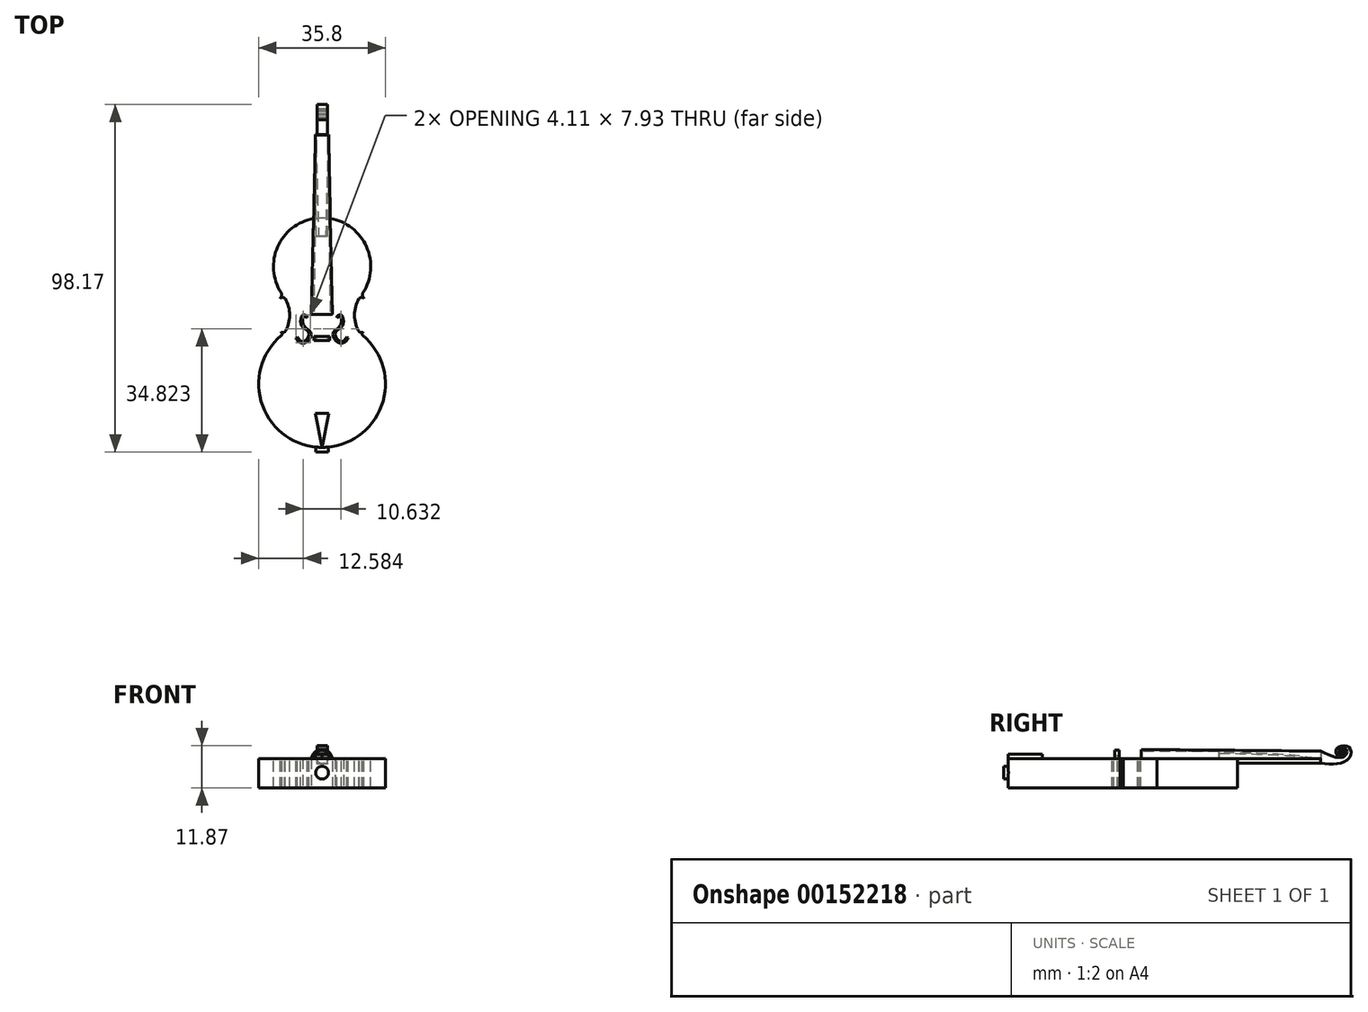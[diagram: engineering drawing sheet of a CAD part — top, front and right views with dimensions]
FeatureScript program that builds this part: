
annotation { "Feature Type Name" : "Feature", "Feature Type Description" : "" }
export const myFeature = defineFeature(function(context is Context, id is Id, definition is map)
    precondition{}
    {
        {
            var Q0;
            Q0=qCreatedBy(makeId("Top.planeOp"),FACE);
            var sketch = newSketch(context, id + "F0", { "sketchPlane" : qUnion([Q0])});
            skArc(sketch, "E0", {"start": v(11.58, 16.32) * mm, "mid": v(0, 37.44) * mm, "end": v(-11.58, 16.32) * mm});
            skArc(sketch, "E1", {"start": v(10.46, 14.69) * mm, "mid": v(9.16, 9.93) * mm, "end": v(10.53, 5.2) * mm});
            skArc(sketch, "E2", {"start": v(-10.53, 5.2) * mm, "mid": v(-9.16, 9.93) * mm, "end": v(-10.46, 14.69) * mm});
            skArc(sketch, "E3", {"start": v(-11.48, 4.23) * mm, "mid": v(0, -27.4) * mm, "end": v(11.48, 4.23) * mm});
            skLineSegment(sketch, "E4", {"start": v(0, -27.4) * mm, "end": v(0, -9.5) * mm, "construction": true});
            skPoint(sketch, "E4.startSnap0", {"position": v(0, -27.4) * mm});
            skLineSegment(sketch, "E5", {"start": v(-3.69, 4.75) * mm, "end": v(-3.08, 4.75) * mm, "construction": true});
            skFitSpline(sketch, "E6", {"points": [v(-4.15, 9.6) * mm, v(-5.44, 10.01) * mm, v(-5.83, 7.1) * mm, v(-3.69, 4.75) * mm, v(-5.3, 2.5) * mm, v(-6.98, 3.84) * mm], "startDerivative": vector(-11.64, 6.4) * mm, "endDerivative": vector(-7.15, 13.02) * mm});
            skFitSpline(sketch, "E7.MirrorCS", {"points": [v(4.15, 9.6) * mm, v(5.44, 10.01) * mm, v(5.83, 7.1) * mm, v(3.69, 4.75) * mm, v(5.3, 2.5) * mm, v(6.98, 3.84) * mm], "startDerivative": vector(11.64, 6.4) * mm, "endDerivative": vector(7.15, 13.02) * mm});
            skLineSegment(sketch, "E8", {"start": v(-4.15, 9.6) * mm, "end": v(-4.15, 9.2) * mm});
            skFitSpline(sketch, "E9", {"points": [v(-4.15, 9.2) * mm, v(-5.28, 9.33) * mm, v(-5.11, 6.98) * mm, v(-3.08, 4.75) * mm, v(-5.3, 1.97) * mm, v(-7.37, 3.53) * mm], "startDerivative": vector(-11.64, 6.4) * mm, "endDerivative": vector(-1.06, 6.87) * mm});
            skLineSegment(sketch, "E10", {"start": v(-7.37, 3.53) * mm, "end": v(-6.98, 3.84) * mm});
            skFitSpline(sketch, "E11.MirrorCS", {"points": [v(4.15, 9.2) * mm, v(5.28, 9.33) * mm, v(5.11, 6.98) * mm, v(3.08, 4.75) * mm, v(5.3, 1.97) * mm, v(7.37, 3.53) * mm], "startDerivative": vector(11.64, 6.4) * mm, "endDerivative": vector(1.06, 6.87) * mm});
            skLineSegment(sketch, "E12.MirrorCS", {"start": v(7.37, 3.53) * mm, "end": v(6.98, 3.84) * mm});
            skLineSegment(sketch, "E13.MirrorCS", {"start": v(4.15, 9.6) * mm, "end": v(4.15, 9.2) * mm});
            skArc(sketch, "E14", {"start": v(-11.9, 14.69) * mm, "mid": v(-11.41, 15.44) * mm, "end": v(-11.58, 16.32) * mm});
            skArc(sketch, "E15", {"start": v(-10.46, 14.69) * mm, "mid": v(-11.18, 14.93) * mm, "end": v(-11.9, 14.69) * mm});
            skArc(sketch, "E16.MirrorCS", {"start": v(11.9, 14.69) * mm, "mid": v(11.41, 15.44) * mm, "end": v(11.58, 16.32) * mm});
            skArc(sketch, "E17.MirrorCS", {"start": v(10.46, 14.69) * mm, "mid": v(11.18, 14.93) * mm, "end": v(11.9, 14.69) * mm});
            skArc(sketch, "E18", {"start": v(-11.53, 4.18) * mm, "mid": v(-11.31, 4.76) * mm, "end": v(-11.76, 5.2) * mm});
            skArc(sketch, "E19", {"start": v(-11.76, 5.2) * mm, "mid": v(-11.14, 5.08) * mm, "end": v(-10.53, 5.2) * mm});
            skArc(sketch, "E20.MirrorCS", {"start": v(11.76, 5.2) * mm, "mid": v(11.14, 5.08) * mm, "end": v(10.53, 5.2) * mm});
            skArc(sketch, "E21.MirrorCS", {"start": v(11.53, 4.18) * mm, "mid": v(11.31, 4.76) * mm, "end": v(11.76, 5.2) * mm});
            skPoint(sketch, "E22.start.orphan", {"position": v(-10.83, 15.26) * mm});
            skLineSegment(sketch, "E23.trimOffspring", {"start": v(3.08, 4.75) * mm, "end": v(3.69, 4.75) * mm, "construction": true});
            skPoint(sketch, "E24.orphan", {"position": v(-10.83, 4.75) * mm});
            skSolve(sketch);
        }
        {
            var Q0;
            Q0=makeQuery(id+"F0.imprint","IMPRINT",FACE,{"disambiguationData":[TD([[makeQuery(id+"F0.imprint","IMPRINT",EDGE,{"derivedFrom":sQuery(id+"F0.wireOp",EDGE,"E0")}),1.0]])]});
            extrude(context, id + "F1", {"entities" : qUnion([Q0]), "oppositeDirection" : true, "depth" : 8.25 * mm});
        }
        {
            var Q0;
            Q0=makeQuery(id+"F0.imprint","IMPRINT",FACE,{"disambiguationData":[TD([[makeQuery(id+"F0.imprint","IMPRINT",EDGE,{"derivedFrom":sQuery(id+"F0.wireOp",EDGE,"E6")}),1.0]])]});
            extrude(context, id + "F2", {"entities" : qUnion([Q0]), "operationType" : NewBodyOperationType.REMOVE, "oppositeDirection" : true, "depth" : 25.4 * mm});
        }
        {
            var Q0;
            Q0=makeQuery(id+"F1.opExtrude","CAP_FACE",FACE,{"disambiguationData":[OSD([sQuery(id+"F0.wireOp",EDGE,"E0"),sQuery(id+"F0.wireOp",EDGE,"E1"),sQuery(id+"F0.wireOp",EDGE,"E2"),sQuery(id+"F0.wireOp",EDGE,"E3"),sQuery(id+"F0.wireOp",EDGE,"E6"),sQuery(id+"F0.wireOp",EDGE,"E7.MirrorCS"),sQuery(id+"F0.wireOp",EDGE,"E8"),sQuery(id+"F0.wireOp",EDGE,"E9"),sQuery(id+"F0.wireOp",EDGE,"E10"),sQuery(id+"F0.wireOp",EDGE,"E11.MirrorCS"),sQuery(id+"F0.wireOp",EDGE,"E12.MirrorCS"),sQuery(id+"F0.wireOp",EDGE,"E13.MirrorCS")])],"isStart":true});
            var sketch = newSketch(context, id + "F3", { "sketchPlane" : qUnion([Q0])});
            skLineSegment(sketch, "E25.bottom", {"start": v(-2.8, 3.95) * mm, "end": v(2.8, 3.95) * mm});
            skLineSegment(sketch, "E25.top", {"start": v(-2.8, 3.43) * mm, "end": v(2.8, 3.43) * mm});
            skLineSegment(sketch, "E25.left", {"start": v(-2.8, 3.95) * mm, "end": v(-2.8, 3.43) * mm});
            skLineSegment(sketch, "E25.right", {"start": v(2.8, 3.95) * mm, "end": v(2.8, 3.43) * mm});
            skLineSegment(sketch, "E26", {"start": v(0, 0) * mm, "end": v(0, 3.95) * mm, "construction": true});
            skSolve(sketch);
        }
        {
            var Q0;
            Q0=makeQuery(id+"F3.imprint","IMPRINT",FACE,{"disambiguationData":[TD([[makeQuery(id+"F3.imprint","IMPRINT",EDGE,{"derivedFrom":sQuery(id+"F3.wireOp",EDGE,"E25.bottom")}),-1.0]])]});
            extrude(context, id + "F4", {"entities" : qUnion([Q0]), "operationType" : NewBodyOperationType.ADD, "depth" : 2.73 * mm});
        }
        {
            var Q0;
            Q0=makeQuery(id+"F4.opExtrude","SWEPT_FACE",FACE,{"disambiguationData":[OSD([sQuery(id+"F3.wireOp",EDGE,"E25.top")])]});
            var sketch = newSketch(context, id + "F5", { "sketchPlane" : qUnion([Q0])});
            skArc(sketch, "E27", {"start": v(1.52, 0) * mm, "mid": v(-0.1, 0.76) * mm, "end": v(-1.7, 0) * mm});
            skSolve(sketch);
        }
        {
            var Q0;
            {var subQ0=sQuery(id+"F5.wireOp",EDGE,"E27");Q0=makeQuery(id+"F5.imprint","IMPRINT",FACE,{"disambiguationData":[TD([[makeQuery(id+"F5.imprint","IMPRINT",EDGE,{"derivedFrom":subQ0}),1.0]])]});}
            extrude(context, id + "F6", {"entities" : qUnion([Q0]), "operationType" : NewBodyOperationType.REMOVE, "oppositeDirection" : true, "depth" : 25.4 * mm});
        }
        {
            var Q0;
            Q0=makeQuery(id+"F4.opExtrude","SWEPT_FACE",FACE,{"disambiguationData":[OSD([sQuery(id+"F3.wireOp",EDGE,"E25.top")])]});
            var sketch = newSketch(context, id + "F7", { "sketchPlane" : qUnion([Q0])});
            skArc(sketch, "E28", {"start": v(2.15, 0) * mm, "mid": v(-0.05, 2.36) * mm, "end": v(-2.25, 0) * mm});
            skSolve(sketch);
        }
        {
            var Q0;
            {var subQ0=sQuery(id+"F7.wireOp",EDGE,"E28");Q0=makeQuery(id+"F7.imprint","IMPRINT",FACE,{"disambiguationData":[TD([[makeQuery(id+"F7.imprint","IMPRINT",EDGE,{"derivedFrom":subQ0}),1.0]])]});}
            extrude(context, id + "F8", {"entities" : qUnion([Q0]), "operationType" : NewBodyOperationType.ADD, "depth" : 0.65 * mm});
        }
        {
            var Q0;
            Q0=makeQuery(id+"F4.opExtrude","SWEPT_FACE",FACE,{"disambiguationData":[OSD([sQuery(id+"F3.wireOp",EDGE,"E25.top")])]});
            extrude(context, id + "F9", {"entities" : qUnion([Q0]), "operationType" : NewBodyOperationType.REMOVE, "oppositeDirection" : true, "depth" : 25.4 * mm});
        }
        {
            var Q0;
            Q0=makeQuery(id+"F8.opExtrude","CAP_FACE",FACE,{"disambiguationData":[OSD([sQuery(id+"F3.wireOp",EDGE,"E25.top"),sQuery(id+"F5.wireOp",EDGE,"E27"),sQuery(id+"F7.wireOp",EDGE,"E28")])],"isStart":false});
            extrude(context, id + "F10", {"entities" : qUnion([Q0]), "operationType" : NewBodyOperationType.ADD, "oppositeDirection" : true, "depth" : 0.3 * mm});
        }
        {
            var Q0;
            Q0=qCreatedBy(makeId("Front.planeOp"),FACE);
            cPlane(context, id + "F11", {"entities" : qUnion([Q0]), "cplaneType" : CPlaneType.OFFSET, "offset" : 27.43 * mm, "width" : 152.4 * mm, "height" : 152.4 * mm});
        }
        {
            var Q0;
            Q0=qCreatedBy(id+"F11.planeOp",FACE);
            var sketch = newSketch(context, id + "F12", { "sketchPlane" : qUnion([Q0])});
            skCircle(sketch, "E29", {"center": v(0, -3.98) * mm, "radius": 1.8 * mm});
            skSolve(sketch);
        }
        {
            var Q0;
            Q0=makeQuery(id+"F12.imprint","IMPRINT",FACE,{"disambiguationData":[TD([[makeQuery(id+"F12.imprint","IMPRINT",EDGE,{"derivedFrom":sQuery(id+"F12.wireOp",EDGE,"E29")}),1.0]])]});
            extrude(context, id + "F13", {"entities" : qUnion([Q0]), "operationType" : NewBodyOperationType.ADD, "endBound" : BoundingType.SYMMETRIC, "depth" : 2.54 * mm});
        }
        {
            var Q0;
            Q0=qCreatedBy(makeId("Front.planeOp"),FACE);
            cPlane(context, id + "F14", {"entities" : qUnion([Q0]), "cplaneType" : CPlaneType.OFFSET, "offset" : 10.16 * mm, "oppositeDirection" : true, "width" : 152.4 * mm, "height" : 152.4 * mm});
        }
        {
            var Q0;
            Q0=qCreatedBy(id+"F14.planeOp",FACE);
            var sketch = newSketch(context, id + "F15", { "sketchPlane" : qUnion([Q0])});
            skArc(sketch, "E30", {"start": v(2.9, 0) * mm, "mid": v(-0.04, 2.57) * mm, "end": v(-3, 0) * mm});
            skArc(sketch, "E31", {"start": v(2.27, 0) * mm, "mid": v(-0.04, 2) * mm, "end": v(-2.36, 0) * mm});
            skLineSegment(sketch, "E32", {"start": v(-0.04, 2.57) * mm, "end": v(-0.04, -0.34) * mm, "construction": true});
            skLineSegment(sketch, "E33", {"start": v(-3, 0) * mm, "end": v(-2.36, 0) * mm});
            skLineSegment(sketch, "E34", {"start": v(2.27, 0) * mm, "end": v(2.9, 0) * mm});
            skSolve(sketch);
        }
        {
            var Q0;
            Q0=qCreatedBy(id+"F14.planeOp",FACE);
            cPlane(context, id + "F16", {"entities" : qUnion([Q0]), "cplaneType" : CPlaneType.OFFSET, "offset" : 50.8 * mm, "oppositeDirection" : true, "width" : 152.4 * mm, "height" : 152.4 * mm});
        }
        {
            var Q0;
            Q0=qCreatedBy(id+"F16.planeOp",FACE);
            var sketch = newSketch(context, id + "F17", { "sketchPlane" : qUnion([Q0])});
            skArc(sketch, "E35", {"start": v(1.84, 0) * mm, "mid": v(0, 2.12) * mm, "end": v(-1.84, 0) * mm});
            skLineSegment(sketch, "E36", {"start": v(1.84, 0) * mm, "end": v(1.64, 0) * mm});
            skLineSegment(sketch, "E37.MirrorCS", {"start": v(-1.84, 0) * mm, "end": v(-1.64, 0) * mm});
            skArc(sketch, "E38", {"start": v(1.64, 0) * mm, "mid": v(0, 1.9) * mm, "end": v(-1.64, 0) * mm});
            skSolve(sketch);
        }
        {
            var Q1;
            Q1=makeQuery(id+"F17.imprint","IMPRINT",FACE,{"disambiguationData":[TD([[makeQuery(id+"F17.imprint","IMPRINT",EDGE,{"derivedFrom":sQuery(id+"F17.wireOp",EDGE,"E35")}),1.0]])]});
            var Q2;
            Q2=makeQuery(id+"F15.imprint","IMPRINT",FACE,{"disambiguationData":[TD([[makeQuery(id+"F15.imprint","IMPRINT",EDGE,{"derivedFrom":sQuery(id+"F15.wireOp",EDGE,"E30")}),1.0]])]});
            loft(context, id + "F18", {"operationType" : NewBodyOperationType.ADD, "sheetProfilesArray" : [{ "sheetProfileEntities" : qUnion([Q1]) }, { "sheetProfileEntities" : qUnion([Q2]) }]});
        }
        {
            var Q0;
            Q0=qCreatedBy(id+"F16.planeOp",FACE);
            var sketch = newSketch(context, id + "F19", { "sketchPlane" : qUnion([Q0])});
            skCircle(sketch, "E39", {"center": v(0, 0.35) * mm, "radius": 1.7 * mm});
            skSolve(sketch);
        }
        {
            var Q0;
            Q0=makeQuery(id+"F19.imprint","IMPRINT",FACE,{"disambiguationData":[TD([[makeQuery(id+"F19.imprint","IMPRINT",EDGE,{"derivedFrom":sQuery(id+"F19.wireOp",EDGE,"E39")}),1.0]])]});
            extrude(context, id + "F20", {"entities" : qUnion([Q0]), "operationType" : NewBodyOperationType.ADD, "depth" : 28.77 * mm});
        }
        {
            var Q0;
            Q0=qCreatedBy(makeId("Right.planeOp"),FACE);
            var sketch = newSketch(context, id + "F21", { "sketchPlane" : qUnion([Q0])});
            skFitSpline(sketch, "E40", {"points": [v(60.84, 2.17) * mm, v(65.9, 0.32) * mm, v(68.17, 1.24) * mm, v(68.06, 2.72) * mm, v(66.86, 2.9) * mm, v(65.9, 2.03) * mm, v(66.52, 1.2) * mm, v(67.55, 1.8) * mm, v(66.72, 2.27) * mm, v(66.69, 1.83) * mm], "startDerivative": vector(25.4, -12.88) * mm, "endDerivative": vector(2.48, -9.98) * mm});
            skFitSpline(sketch, "E41", {"points": [v(60.88, -1.33) * mm, v(66.28, -1.33) * mm, v(69.23, 0.62) * mm, v(69, 3.13) * mm, v(66.93, 3.55) * mm, v(65.28, 2.58) * mm, v(65.45, 1.1) * mm, v(67.57, 0.94) * mm], "startDerivative": vector(27.47, -2.66) * mm, "endDerivative": vector(19.52, -0.18) * mm});
            skLineSegment(sketch, "E42", {"start": v(60.84, 2.17) * mm, "end": v(60.88, -1.33) * mm});
            skFitSpline(sketch, "E43", {"points": [v(67.57, 0.94) * mm, v(67.84, 1.19) * mm, v(67.96, 1.78) * mm, v(67.63, 2.3) * mm, v(67.16, 2.5) * mm, v(66.63, 2.47) * mm, v(66.41, 2.15) * mm, v(66.4, 1.77) * mm, v(66.6, 1.53) * mm, v(66.79, 1.58) * mm, v(66.69, 1.83) * mm], "startDerivative": vector(3.02, 2.07) * mm, "endDerivative": vector(-2.37, 3.43) * mm});
            skSolve(sketch);
        }
        {
            var Q0;
            Q0=makeQuery(id+"F21.imprint","IMPRINT",FACE,{"disambiguationData":[TD([[makeQuery(id+"F21.imprint","IMPRINT",EDGE,{"derivedFrom":sQuery(id+"F21.wireOp",EDGE,"E40")}),-1.0]])]});
            extrude(context, id + "F22", {"entities" : qUnion([Q0]), "endBound" : BoundingType.SYMMETRIC, "oppositeDirection" : true, "depth" : 2.92 * mm});
        }
        {
            var Q0;
            {var subQ1=sQuery(id+"F3.wireOp",EDGE,"E25.top");var subQ3=makeQuery(id+"F1.opExtrude","CAP_FACE",FACE,{"disambiguationData":[OSD([sQuery(id+"F0.wireOp",EDGE,"E0"),sQuery(id+"F0.wireOp",EDGE,"E1"),sQuery(id+"F0.wireOp",EDGE,"E2"),sQuery(id+"F0.wireOp",EDGE,"E3"),sQuery(id+"F0.wireOp",EDGE,"E6"),sQuery(id+"F0.wireOp",EDGE,"E7.MirrorCS"),sQuery(id+"F0.wireOp",EDGE,"E8"),sQuery(id+"F0.wireOp",EDGE,"E9"),sQuery(id+"F0.wireOp",EDGE,"E10"),sQuery(id+"F0.wireOp",EDGE,"E11.MirrorCS"),sQuery(id+"F0.wireOp",EDGE,"E12.MirrorCS"),sQuery(id+"F0.wireOp",EDGE,"E13.MirrorCS"),sQuery(id+"F0.wireOp",EDGE,"E14"),sQuery(id+"F0.wireOp",EDGE,"E15"),sQuery(id+"F0.wireOp",EDGE,"E16.MirrorCS"),sQuery(id+"F0.wireOp",EDGE,"E17.MirrorCS"),sQuery(id+"F0.wireOp",EDGE,"E18"),sQuery(id+"F0.wireOp",EDGE,"E19"),sQuery(id+"F0.wireOp",EDGE,"E20.MirrorCS"),sQuery(id+"F0.wireOp",EDGE,"E21.MirrorCS")])],"isStart":true});var subQ4=makeQuery(id+"F6.opExtrude","SWEPT_FACE",FACE,{"disambiguationData":[OSD([subQ1])]});var subQ5=makeQuery(id+"F4.opExtrude","CAP_EDGE",EDGE,{"disambiguationData":[OSD([subQ1])],"isStart":true});Q0=makeQuery(id+"F9.boolean.opBoolean","MERGE",FACE,{"derivedFrom":[makeQuery(id+"F6.boolean.opBoolean","MERGE",FACE,{"derivedFrom":[subQ3,subQ4]}),makeQuery(id+"F9.opExtrude","SWEPT_FACE",FACE,{"disambiguationData":[OSD([subQ1]),TDD([makeQuery(id+"F6.boolean.opBoolean","SPLIT",EDGE,{"disambiguationData":[TD([makeQuery(id+"F4.opExtrude","SWEPT_FACE",FACE,{"disambiguationData":[OSD([sQuery(id+"F3.wireOp",EDGE,"E25.left")])]})])],"derivedFrom":subQ5})])]}),makeQuery(id+"F9.opExtrude","SWEPT_FACE",FACE,{"disambiguationData":[OSD([subQ1]),TDD([makeQuery(id+"F6.boolean.opBoolean","SPLIT",EDGE,{"disambiguationData":[TD([makeQuery(id+"F4.opExtrude","SWEPT_FACE",FACE,{"disambiguationData":[OSD([sQuery(id+"F3.wireOp",EDGE,"E25.right")])]})])],"derivedFrom":subQ5})])]})]});}
            var sketch = newSketch(context, id + "F23", { "sketchPlane" : qUnion([Q0])});
            skLineSegment(sketch, "E44", {"start": v(0, -27.4) * mm, "end": v(-1.96, -17.76) * mm});
            skLineSegment(sketch, "E45.MirrorCS", {"start": v(0, -27.4) * mm, "end": v(1.96, -17.76) * mm});
            skLineSegment(sketch, "E46", {"start": v(-1.96, -17.76) * mm, "end": v(1.96, -17.76) * mm});
            skSolve(sketch);
        }
        {
            var Q0;
            Q0=makeQuery(id+"F23.imprint","IMPRINT",FACE,{"disambiguationData":[TD([[makeQuery(id+"F23.imprint","IMPRINT",EDGE,{"derivedFrom":sQuery(id+"F23.wireOp",EDGE,"E44")}),-1.0]])]});
            extrude(context, id + "F24", {"entities" : qUnion([Q0]), "operationType" : NewBodyOperationType.ADD, "depth" : 1.27 * mm});
        }
    });
